# Revit family: IS_ConnectAir_A7007_BIM_DE
name_source: partatom
category: Plumbing Fixtures
revit_build: Autodesk Revit MEP 2015 (Build: 20140606_1530(x64)
units: mm (PartAtom-declared; Revit-internal decimal feet)

## types (1)
- A7007AA - Connect Air Basin Mixer  Slim Pu/M
    BIMobject category = Taps & Mixers
    BOSUseNativeGeometries = 1
    Brand url = www.idealstandard.com
    EAN code = https://4015413340632
    Edition number = 1
    Installation instructions = www.idealstandard.de\produkte
    Manufacturer name = Ideal Standard
    Material main = Brass
    Model = A7007AA
    Nominal height = 72
    Nominal width = 185
    Product Guid = fc469220-3d47-4be9-9d0c-7008f638340f
    Product SKU = A7007
    Product data url = https://bimobject.com
    Product name = Connect Air Basin Mixer  Slim Pu/M
    Product url = http://www.idealspec.co.uk
    QR code = http://bimobject.com
    Technical description = http://www.idealspec.co.uk
    Uniclass 2015 Code = Pr_40_20_87_98
    Uniclass 2015 Name = Washbasin taps
    Weight Net (Kg) = 0

## geometry (parser evidence)
native form markers: Blend x4, Sweep x1
no freeform markers — native parametric forms only
